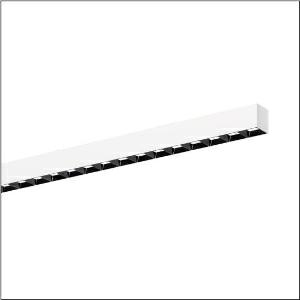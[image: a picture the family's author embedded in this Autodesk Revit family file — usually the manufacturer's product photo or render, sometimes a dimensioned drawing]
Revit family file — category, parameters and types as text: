
# Revit family: silica_21_51mx21tctaw
name_source: partatom
category: Lighting Fixtures
units: mm (PartAtom-declared; Revit-internal decimal feet)

## family parameters
Cut with Voids When Loaded = No
Host = Face
Light Source = No
Part Type = Normal
Room Calculation Point = No
Round Connector Dimension = Use Diameter
Shared = No

## types (1)
- --- (1 x LED, 9300 lm, 80.5 W, 6500K)
    Apparent Load = 81 VA
    CIE Flux Codes = 85 99 100 100 100
    Color Rendering = 80
    Color Temperature = 6500K
    Default Elevation = 1800 mm
    Description = Silica 21, office luminaire, primary light control with darklight reflector, of PMMA, black, CAT 2 (L<= 3000cd/m²), light emission: direct distribution, primary light characteristic: symmetric, installation type: surface-mounted, LED, rated luminous flux: 9.300lm, luminous efficacy: 110lm/W, light colour: 8tw, colour temperature: 2700..6500K, control gear: DALI DT8, with terminal, 3+2-pole, max. 2.5mm², mains connection: 220..240V, AC, 50/60Hz, rated input power: 84.6W, luminaire housing, of aluminium, traffic white (RAL 9016), length: 3.004mm, width: 53mm, height: 53mm, protection rating (complete): IP20, insulation class (complete): insulation class I (protective earthing), certification: CE, permissible operating ambient temperature: 0..+35°C, standard: EN 50419, packaging unit: 1 piece
    Height = 53 mm
    Lamp = 1 x LED
    Lamp Light Flux = 9300 lm
    Lamp Power = 80.5 W
    Lamp count = 1
    Length = 3004 mm
    Luminous efficacy = 116 lm/W
    Manufacturer = Siteco
    ModVariant = No
    Model = 51MX21TCTAW
    Mounting Place = Ceiling
    Mounting Type = Surface mounted
    Number of Poles = 1
    OnlyDefault = Yes
    Power Factor = 1
    Product Name = Silica 21
    Product group = office luminaire | ceiling mounted
    ProductGroupID = 301
    Protection Class = Protection class I
    Protection Degree = IP 20
    RLX_Detail_Level = 1
    RLX_Emergency_Light_Flux = 0 lm
    RLX_Emergency_Type = 0
    RLX_Emergency_Type_DB = No
    RlxData = <blob elided: 58549 chars, md5=1c79b6da>
    Socket = socket
    Standby Power = 0 W
    System Light Flux = 9300 lm
    System Power = 81 W
    Type Comments = individual setting
    Type Image = l_1335873.jpg
    URL = http://relux.com
    VarID = @adj_141127
    Voltage = 0 V
    Weight = 0.00 kg
    Width = 53 mm

## geometry (parser evidence)
native form markers: Blend x4, Sweep x12
no freeform markers — native parametric forms only
